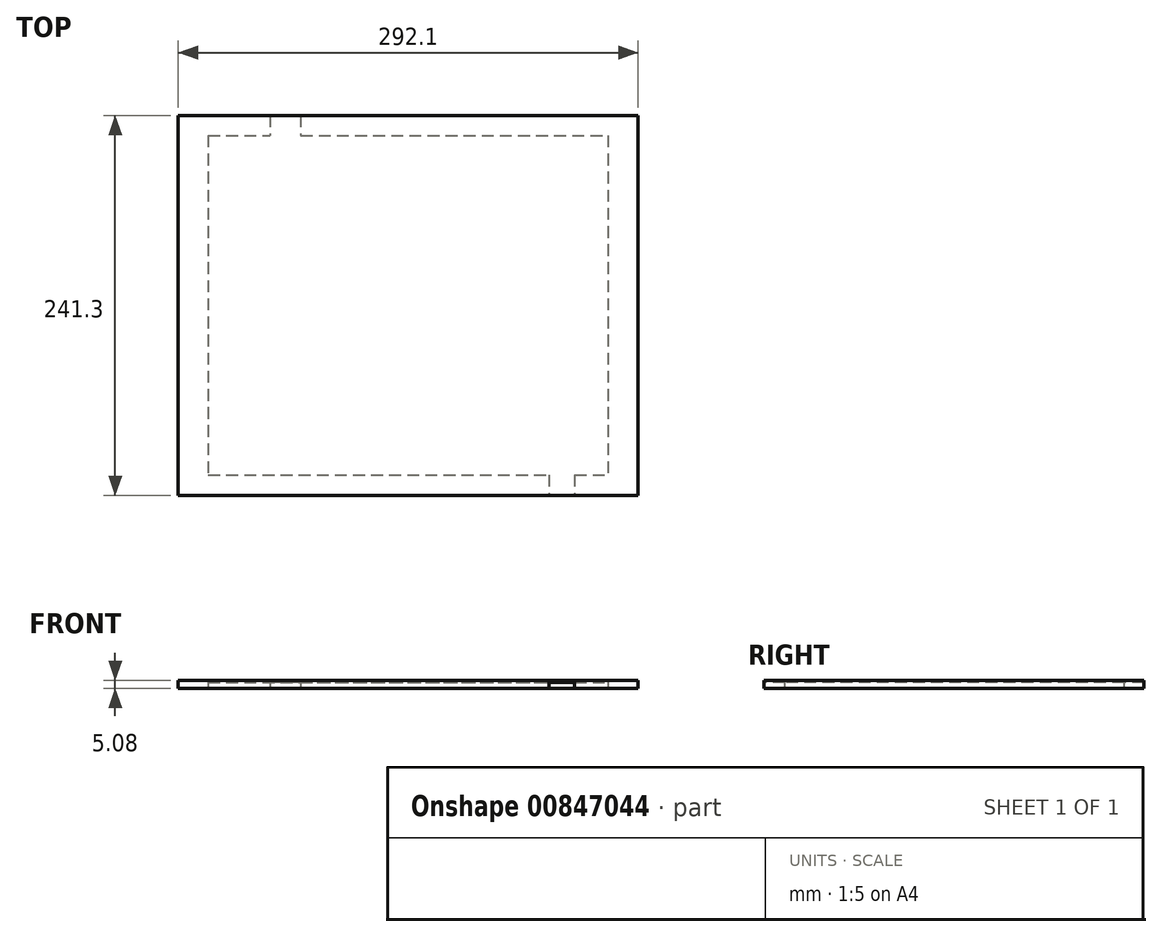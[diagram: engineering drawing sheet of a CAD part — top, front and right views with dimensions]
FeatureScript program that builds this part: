
annotation { "Feature Type Name" : "Feature", "Feature Type Description" : "" }
export const myFeature = defineFeature(function(context is Context, id is Id, definition is map)
    precondition{}
    {
        {
            var Q0;
            Q0=qCreatedBy(makeId("Top.planeOp"),FACE);
            var sketch = newSketch(context, id + "F0", { "sketchPlane" : qUnion([Q0])});
            skLineSegment(sketch, "E0.bottom", {"start": v(146.84, 120.36) * mm, "end": v(-145.26, 120.36) * mm});
            skLineSegment(sketch, "E0.top", {"start": v(146.84, -120.94) * mm, "end": v(-145.26, -120.94) * mm});
            skLineSegment(sketch, "E0.left", {"start": v(146.84, 120.36) * mm, "end": v(146.84, -120.94) * mm});
            skLineSegment(sketch, "E0.right", {"start": v(-145.26, 120.36) * mm, "end": v(-145.26, -120.94) * mm});
            skLineSegment(sketch, "E1.right", {"start": v(-126.2, -44.38) * mm, "end": v(-126.2, -107.88) * mm});
            skLineSegment(sketch, "E2.top", {"start": v(90.2, -122.1) * mm, "end": v(106.59, -122.1) * mm});
            skLineSegment(sketch, "E2.left", {"start": v(90.2, -107.83) * mm, "end": v(90.2, -122.1) * mm});
            skLineSegment(sketch, "E2.right", {"start": v(106.59, -107.83) * mm, "end": v(106.59, -122.1) * mm});
            skLineSegment(sketch, "E3.bottom", {"start": v(-126.2, 107.66) * mm, "end": v(127.8, 107.66) * mm});
            skLineSegment(sketch, "E3.top", {"start": v(-126.2, -107.88) * mm, "end": v(127.8, -107.88) * mm});
            skLineSegment(sketch, "E3.left", {"start": v(-126.2, 107.66) * mm, "end": v(-126.2, -107.88) * mm});
            skLineSegment(sketch, "E3.right", {"start": v(127.8, 107.66) * mm, "end": v(127.8, -107.88) * mm});
            skLineSegment(sketch, "E4.bottom", {"start": v(-86.94, 123.04) * mm, "end": v(-67.42, 123.04) * mm});
            skLineSegment(sketch, "E4.top", {"start": v(-86.94, 105.1) * mm, "end": v(-67.42, 105.1) * mm});
            skLineSegment(sketch, "E4.left", {"start": v(-86.94, 123.04) * mm, "end": v(-86.94, 105.1) * mm});
            skLineSegment(sketch, "E4.right", {"start": v(-67.42, 123.04) * mm, "end": v(-67.42, 105.1) * mm});
            skSolve(sketch);
        }
        {
            var Q0;
            {var subQ0=sQuery(id+"F0.wireOp",EDGE,"E0.right");Q0=makeQuery(id+"F0.imprint","IMPRINT",FACE,{"disambiguationData":[TD([[makeQuery(id+"F0.imprint","IMPRINT",EDGE,{"derivedFrom":subQ0}),1.0]])]});}
            var Q1;
            {var subQ5=sQuery(id+"F0.wireOp",EDGE,"E0.left");Q1=makeQuery(id+"F0.imprint","IMPRINT",FACE,{"disambiguationData":[TD([[makeQuery(id+"F0.imprint","IMPRINT",EDGE,{"derivedFrom":subQ5}),-1.0]])]});}
            var Q2;
            {var subQ0=sQuery(id+"F0.wireOp",EDGE,"E4.left");var subQ1=sQuery(id+"F0.wireOp",EDGE,"E0.bottom");var subQ2=makeQuery(id+"F0.imprint","INTERSECT",VERTEX,{"derivedFrom":[subQ1,subQ0]});Q2=makeQuery(id+"F0.imprint","IMPRINT",FACE,{"disambiguationData":[TD([[makeQuery(id+"F0.imprint","IMPRINT",EDGE,{"disambiguationData":[TD([[subQ2,1.0]])],"derivedFrom":subQ1}),1.0]])]});}
            var Q3;
            {var subQ0=sQuery(id+"F0.wireOp",EDGE,"E2.left");var subQ1=sQuery(id+"F0.wireOp",EDGE,"E0.top");var subQ2=makeQuery(id+"F0.imprint","INTERSECT",VERTEX,{"derivedFrom":[subQ1,subQ0]});Q3=makeQuery(id+"F0.imprint","IMPRINT",FACE,{"disambiguationData":[TD([[makeQuery(id+"F0.imprint","IMPRINT",EDGE,{"disambiguationData":[TD([[subQ2,1.0]])],"derivedFrom":subQ1}),-1.0]])]});}
            extrude(context, id + "F1", {"entities" : qUnion([Q0, Q1, Q2, Q3]), "depth" : 5.08 * mm, "offsetDistance" : 25.4 * mm});
        }
        {
            var Q0;
            {var subQ6=sQuery(id+"F0.wireOp",EDGE,"E1.right");Q0=makeQuery(id+"F0.imprint","IMPRINT",FACE,{"disambiguationData":[TD([[makeQuery(id+"F0.imprint","IMPRINT",EDGE,{"derivedFrom":subQ6}),1.0]])]});}
            var Q1;
            {var subQ5=sQuery(id+"F0.wireOp",EDGE,"E4.top");Q1=makeQuery(id+"F0.imprint","IMPRINT",FACE,{"disambiguationData":[TD([[makeQuery(id+"F0.imprint","IMPRINT",EDGE,{"derivedFrom":subQ5}),1.0]])]});}
            extrude(context, id + "F2", {"entities" : qUnion([Q0, Q1]), "operationType" : NewBodyOperationType.ADD, "depth" : 5.08 * mm, "offsetDistance" : 25.4 * mm});
        }
        {
            var Q0;
            {var subQ6=sQuery(id+"F0.wireOp",EDGE,"E1.right");Q0=makeQuery(id+"F0.imprint","IMPRINT",FACE,{"disambiguationData":[TD([[makeQuery(id+"F0.imprint","IMPRINT",EDGE,{"derivedFrom":subQ6}),1.0]])]});}
            var Q1;
            {var subQ5=sQuery(id+"F0.wireOp",EDGE,"E4.top");Q1=makeQuery(id+"F0.imprint","IMPRINT",FACE,{"disambiguationData":[TD([[makeQuery(id+"F0.imprint","IMPRINT",EDGE,{"derivedFrom":subQ5}),1.0]])]});}
            extrude(context, id + "F3", {"entities" : qUnion([Q0, Q1]), "operationType" : NewBodyOperationType.REMOVE, "oppositeDirection" : true, "depth" : -3.8 * mm, "offsetDistance" : 25.4 * mm});
        }
        {
            var Q0;
            {var subQ0=sQuery(id+"F0.wireOp",EDGE,"E2.left");var subQ1=sQuery(id+"F0.wireOp",EDGE,"E0.top");var subQ2=makeQuery(id+"F0.imprint","INTERSECT",VERTEX,{"derivedFrom":[subQ1,subQ0]});Q0=makeQuery(id+"F0.imprint","IMPRINT",FACE,{"disambiguationData":[TD([[makeQuery(id+"F0.imprint","IMPRINT",EDGE,{"disambiguationData":[TD([[subQ2,1.0]])],"derivedFrom":subQ1}),-1.0]])]});}
            var Q1;
            {var subQ0=sQuery(id+"F0.wireOp",EDGE,"E4.left");var subQ1=sQuery(id+"F0.wireOp",EDGE,"E0.bottom");var subQ2=makeQuery(id+"F0.imprint","INTERSECT",VERTEX,{"derivedFrom":[subQ1,subQ0]});Q1=makeQuery(id+"F0.imprint","IMPRINT",FACE,{"disambiguationData":[TD([[makeQuery(id+"F0.imprint","IMPRINT",EDGE,{"disambiguationData":[TD([[subQ2,1.0]])],"derivedFrom":subQ1}),1.0]])]});}
            extrude(context, id + "F4", {"entities" : qUnion([Q0, Q1]), "operationType" : NewBodyOperationType.REMOVE, "oppositeDirection" : true, "depth" : -3.8 * mm, "offsetDistance" : 25.4 * mm});
        }
    });
